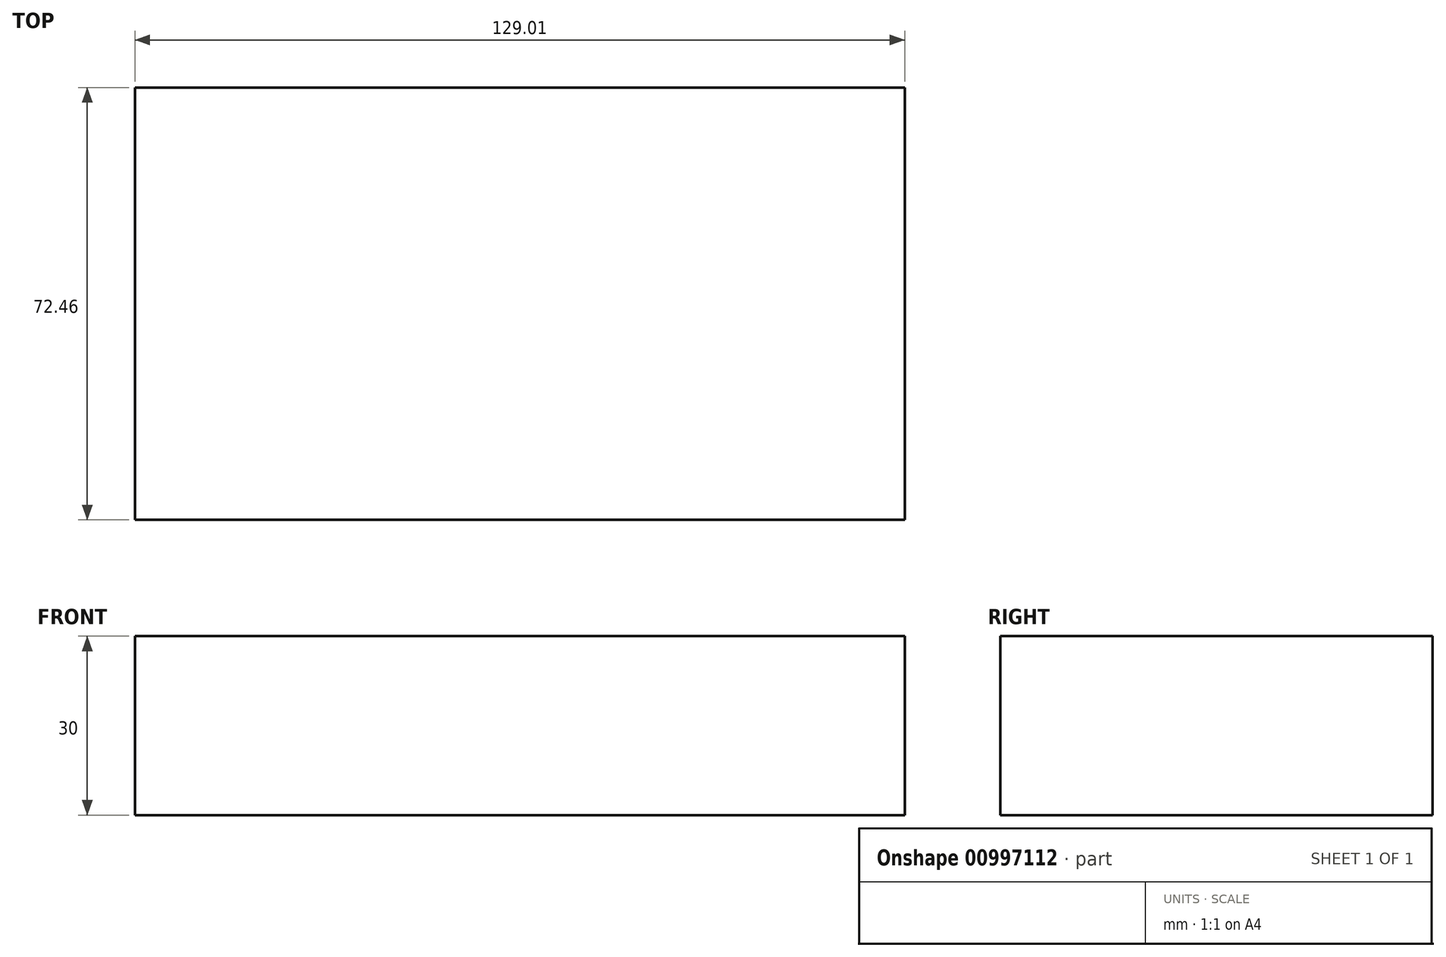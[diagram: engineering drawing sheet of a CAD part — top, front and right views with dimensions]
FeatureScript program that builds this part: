
annotation { "Feature Type Name" : "Feature", "Feature Type Description" : "" }
export const myFeature = defineFeature(function(context is Context, id is Id, definition is map)
    precondition{}
    {
        {
            var Q0;
            Q0=qCreatedBy(makeId("Top.planeOp"),FACE);
            var sketch = newSketch(context, id + "F0", { "sketchPlane" : qUnion([Q0])});
            skLineSegment(sketch, "E0.bottom", {"start": v(-72.68, 30.84) * mm, "end": v(56.33, 30.84) * mm});
            skLineSegment(sketch, "E0.top", {"start": v(-72.68, -41.62) * mm, "end": v(56.33, -41.62) * mm});
            skLineSegment(sketch, "E0.left", {"start": v(-72.68, 30.84) * mm, "end": v(-72.68, -41.62) * mm});
            skLineSegment(sketch, "E0.right", {"start": v(56.33, 30.84) * mm, "end": v(56.33, -41.62) * mm});
            skSolve(sketch);
        }
        {
            var Q0;
            Q0=makeQuery(id+"F0.imprint","IMPRINT",FACE,{"disambiguationData":[TD([[makeQuery(id+"F0.imprint","IMPRINT",EDGE,{"derivedFrom":sQuery(id+"F0.wireOp",EDGE,"E0.bottom")}),-1.0]])]});
            extrude(context, id + "F1", {"entities" : qUnion([Q0]), "depth" : 30 * mm, "offsetDistance" : 25 * mm});
        }
    });
